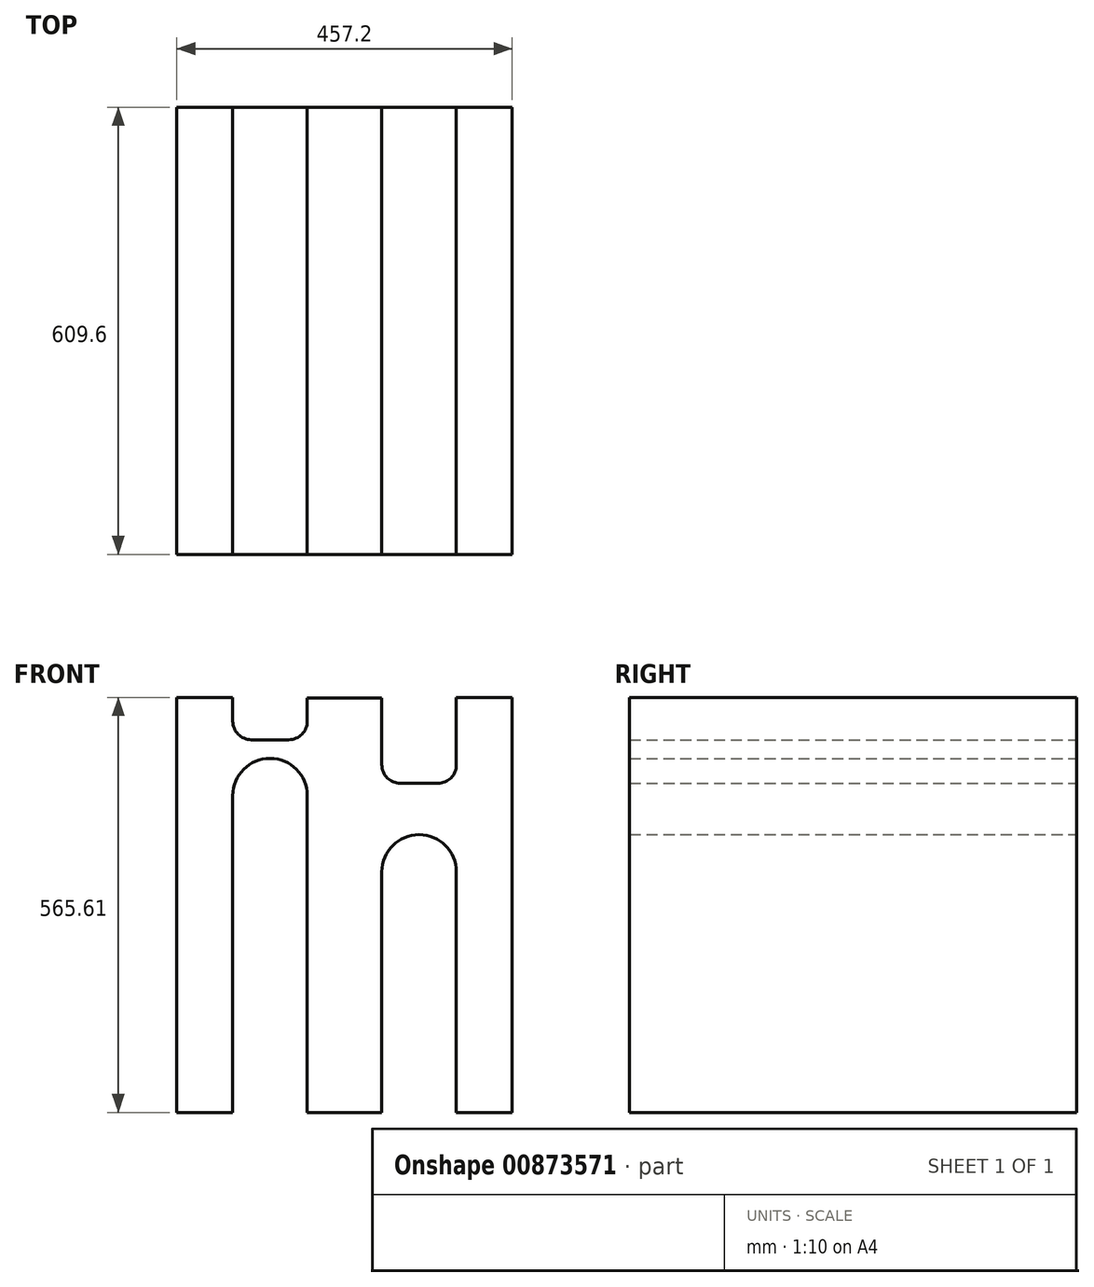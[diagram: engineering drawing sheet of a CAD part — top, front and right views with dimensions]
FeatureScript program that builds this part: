
annotation { "Feature Type Name" : "Feature", "Feature Type Description" : "" }
export const myFeature = defineFeature(function(context is Context, id is Id, definition is map)
    precondition{}
    {
        {
            var Q0;
            Q0=qCreatedBy(makeId("Front.planeOp"),FACE);
            var sketch = newSketch(context, id + "F0", { "sketchPlane" : qUnion([Q0])});
            skLineSegment(sketch, "E0.bottom", {"start": v(0, 0) * mm, "end": v(76.2, 0) * mm});
            skLineSegment(sketch, "E0.top", {"start": v(0, 431.8) * mm, "end": v(228.6, 431.8) * mm, "construction": true});
            skLineSegment(sketch, "E0.left", {"start": v(0, 0) * mm, "end": v(0, 431.8) * mm});
            skLineSegment(sketch, "E1", {"start": v(228.6, 0) * mm, "end": v(228.6, 355.6) * mm, "construction": true});
            skLineSegment(sketch, "E2.0", {"start": v(76.2, 0) * mm, "end": v(76.2, 431.8) * mm});
            skLineSegment(sketch, "E3.0", {"start": v(127, 482.6) * mm, "end": v(127, 482.6) * mm});
            skArc(sketch, "E4.filletArc", {"start": v(127, 482.6) * mm, "mid": v(91.08, 467.72) * mm, "end": v(76.2, 431.8) * mm});
            skLineSegment(sketch, "E5.0", {"start": v(177.8, 0) * mm, "end": v(177.8, 431.8) * mm});
            skArc(sketch, "E6.filletArc", {"start": v(177.8, 431.8) * mm, "mid": v(162.92, 467.72) * mm, "end": v(127, 482.6) * mm});
            skLineSegment(sketch, "E7.trimOffspring", {"start": v(177.8, 0) * mm, "end": v(279.4, 0) * mm});
            skLineSegment(sketch, "E8.trimOffspring", {"start": v(381, 0) * mm, "end": v(457.2, 0) * mm});
            skLineSegment(sketch, "E9", {"start": v(0, 431.8) * mm, "end": v(0, 565.6) * mm});
            skPoint(sketch, "E10.endSnap0", {"position": v(228.6, 431.8) * mm});
            skLineSegment(sketch, "E11", {"start": v(76.2, 565.6) * mm, "end": v(0, 565.6) * mm});
            skPoint(sketch, "E12.orphan", {"position": v(0, 609.6) * mm});
            skLineSegment(sketch, "E13.MirrorCS", {"start": v(381, 565.6) * mm, "end": v(457.2, 565.6) * mm});
            skPoint(sketch, "E14.top.start.orphan", {"position": v(211.47, 448.29) * mm});
            skLineSegment(sketch, "E15", {"start": v(177.8, 564.99) * mm, "end": v(279.4, 564.99) * mm});
            skPoint(sketch, "E16.MirrorCS.start.orphan", {"position": v(381, 565.6) * mm});
            skLineSegment(sketch, "E17", {"start": v(457.2, 565.6) * mm, "end": v(457.2, 0) * mm});
            skLineSegment(sketch, "E18", {"start": v(279.4, 564.99) * mm, "end": v(279.4, 473.94) * mm});
            skLineSegment(sketch, "E19", {"start": v(304.8, 448.54) * mm, "end": v(355.6, 448.54) * mm});
            skLineSegment(sketch, "E20", {"start": v(381, 473.94) * mm, "end": v(381, 565.6) * mm});
            skPoint(sketch, "E21.visualSharp", {"position": v(279.4, 448.54) * mm});
            skArc(sketch, "E21.filletArc", {"start": v(279.4, 473.94) * mm, "mid": v(286.84, 455.98) * mm, "end": v(304.8, 448.54) * mm});
            skPoint(sketch, "E22.visualSharp", {"position": v(381, 448.54) * mm});
            skArc(sketch, "E22.filletArc", {"start": v(355.6, 448.54) * mm, "mid": v(373.56, 455.98) * mm, "end": v(381, 473.94) * mm});
            skLineSegment(sketch, "E23", {"start": v(279.4, 0) * mm, "end": v(279.4, 327.89) * mm});
            skLineSegment(sketch, "E24", {"start": v(330.2, 378.69) * mm, "end": v(330.2, 378.69) * mm});
            skLineSegment(sketch, "E25", {"start": v(381, 327.89) * mm, "end": v(381, 0) * mm});
            skPoint(sketch, "E26.visualSharp", {"position": v(279.4, 378.69) * mm});
            skArc(sketch, "E26.filletArc", {"start": v(330.2, 378.69) * mm, "mid": v(294.28, 363.8) * mm, "end": v(279.4, 327.89) * mm});
            skPoint(sketch, "E27.visualSharp", {"position": v(381, 378.69) * mm});
            skArc(sketch, "E27.filletArc", {"start": v(381, 327.89) * mm, "mid": v(366.12, 363.8) * mm, "end": v(330.2, 378.69) * mm});
            skLineSegment(sketch, "E28", {"start": v(76.2, 565.6) * mm, "end": v(76.2, 533.4) * mm});
            skLineSegment(sketch, "E29", {"start": v(101.6, 508) * mm, "end": v(152.4, 508) * mm});
            skLineSegment(sketch, "E30", {"start": v(177.8, 533.4) * mm, "end": v(177.8, 564.99) * mm});
            skPoint(sketch, "E31.visualSharp", {"position": v(76.2, 508) * mm});
            skArc(sketch, "E31.filletArc", {"start": v(76.2, 533.4) * mm, "mid": v(83.64, 515.44) * mm, "end": v(101.6, 508) * mm});
            skPoint(sketch, "E32.visualSharp", {"position": v(177.8, 508) * mm});
            skArc(sketch, "E32.filletArc", {"start": v(152.4, 508) * mm, "mid": v(170.36, 515.44) * mm, "end": v(177.8, 533.4) * mm});
            skSolve(sketch);
        }
        {
            var Q0;
            Q0 = qSketchRegion(id + "F0", true);
            extrude(context, id + "F1", {"entities" : qUnion([Q0]), "depth" : 609.6 * mm, "offsetDistance" : 25.4 * mm});
        }
    });
